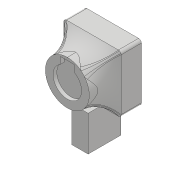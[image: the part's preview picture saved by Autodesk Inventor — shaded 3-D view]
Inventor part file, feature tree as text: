
AUTODESK INVENTOR PART (.ipt)
format: ipt  version: 2018 (Build 220112000, 112)  size: 754,176 bytes
history: native  units: mm
features: sketch x32, extrude x28, projected_geometry x28, fillet x4, hole x3, chamfer x1, mirror x1, revolve x1
ambient origin geometry x8: Origin, YZ Plane, XZ Plane, XY Plane, X Axis, Y Axis, Z Axis, Center Point
bodies: Solid1 (feature_tree)
feature tree (98):
  extrude  "Extrusion1"  Depth=45.0mm
  extrude  "Extrusion2"  Depth=2.25mm
  hole  "Hole1"  [1 undecoded]
  hole  "Hole2"  [1 undecoded]
  fillet  "Fillet1"  Radius=14.0mm
  extrude  "Extrusion3"  Depth=18.5mm
  extrude  "Extrusion4"  Depth=20.5mm
  extrude  "Extrusion5"  Depth=2.195mm
  extrude  "Extrusion6"  Depth=20.5mm
  hole  "Hole3"  [1 undecoded]
  extrude  "Extrusion7"  Depth=0.5mm
  extrude  "Extrusion8"  Depth=5.0mm TaperAngle=0.0deg
  extrude  "Extrusion9"  Depth=24.5mm
  extrude  "Extrusion10"  Depth=10.0mm
  extrude  "Extrusion11"  Depth=14.5mm
  extrude  "Extrusion12"  Depth=14.5mm
  extrude  "Extrusion13"  Depth=5.0mm
  extrude  "Extrusion14"  Depth=2.25mm
  extrude  "Extrusion15"  Depth=5.0mm
  extrude  "Extrusion16"  Depth=9.0mm
  extrude  "Extrusion17"  Depth=4.0mm
  chamfer  "Chamfer1"  Distance=1.0mm
  fillet  "Fillet8"  Radius=20.7mm
  mirror  "Mirror1"
  extrude  "Extrusion18"  Depth=32.0mm
  extrude  "Extrusion19"  Depth=1.0mm TaperAngle=0.0deg
  extrude  "Extrusion20"  Depth=8.0mm
  extrude  "Extrusion21"  Depth=0.2mm TaperAngle=0.0deg
  extrude  "Extrusion22"  Depth=0.5mm TaperAngle=0.0deg
  extrude  "Extrusion23"  Depth=3.0mm TaperAngle=0.0deg
  extrude  "Extrusion24"  Depth=0.2mm TaperAngle=0.0deg
  sketch  "Sketch35"  dims[d91=8.0mm d92=0.0mm d93=3.0mm d94=0.0mm]
  revolve  "Revolution1"  Angle=45.0deg
  extrude  "Extrusion25"  Depth=22.55mm TaperAngle=0.0deg
  fillet  "Fillet11"  Radius=4.0mm
  fillet  "Fillet14"  Radius=4.0mm
  extrude  "Extrusion33"  Depth=30.0mm
  extrude  "Extrusion34"  Depth=30.0mm TaperAngle=0.0deg
  extrude  "Extrusion35"  Depth=30.0mm
  sketch  "Sketch1"  dims[d0=24.5mm d1=45.0mm]
  sketch  "Sketch2"  dims[d2=1.95mm d3=0.0mm d4=2.25mm]
  projected_geometry  "Projected Loop1"
  sketch  "Sketch3"  dims[d5=20.0mm d6=2.25mm]
  projected_geometry  "Projected Loop2"
  sketch  "Sketch4"  dims[d7=5.25mm d8=5.25mm d9=14.0mm]
  projected_geometry  "Projected Loop3"
  sketch  "Sketch5"  dims[d10=5.25mm d11=18.5mm]
  projected_geometry  "Projected Loop4"
  sketch  "Sketch6"  dims[d12=10.0mm d13=0.0mm d14=20.5mm]
  projected_geometry  "Projected Loop5"
  sketch  "Sketch7"  dims[d15=2.0mm d16=2.195mm]
  projected_geometry  "Projected Loop6"
  sketch  "Sketch8"  dims[d17=2.0mm]
  projected_geometry  "Projected Loop7"
  sketch  "Sketch9"  dims[d18=2.4mm d19=6.0mm d20=4.4mm d21=2.0mm d22=90.0deg d23=8.0mm d24=20.594885mm d25=20.5mm]
  projected_geometry  "Projected Loop8"
  projected_geometry  "Projected Loop9"
  sketch  "Sketch10"  dims[d26=26.65mm d27=2.0mm]
  projected_geometry  "Projected Loop10"
  projected_geometry  "Projected Loop11"
  sketch  "Sketch11"  dims[d28=2.0mm]
  projected_geometry  "Projected Loop12"
  sketch  "Sketch12"  dims[d29=2.4mm d30=6.0mm d31=4.4mm d32=2.0mm d33=90.0deg d34=8.0mm d35=20.594885mm d36=0.5mm]
  sketch  "Sketch13"  dims[d37=18.0mm d38=5.0mm d39=0.0mm]
  sketch  "Sketch14"  dims[d41=10.0mm d42=0.0mm d43=24.5mm]
  projected_geometry  "Projected Loop13"
  sketch  "Sketch15"  dims[d44=1.15mm d45=0.0mm d46=10.0mm]
  sketch  "Sketch16"  dims[d47=21.0mm d48=14.5mm]
  projected_geometry  "Projected Loop14"
  sketch  "Sketch17"  dims[d49=20.0mm d50=14.5mm]
  projected_geometry  "Projected Loop15"
  sketch  "Sketch18"  dims[d51=24.5mm d52=5.0mm]
  projected_geometry  "Projected Loop16"
  sketch  "Sketch19"  dims[d53=5.0mm d54=2.25mm]
  projected_geometry  "Projected Loop17"
  sketch  "Sketch20"  dims[d55=2.25mm d56=5.0mm]
  projected_geometry  "Projected Loop18"
  sketch  "Sketch22"  dims[d57=5.0mm d58=9.0mm]
  sketch  "Sketch25"  dims[d59=14.75mm d60=4.0mm d61=1.0mm d62=0.0mm d63=20.7mm]
  sketch  "Sketch27"  dims[d64=2.4mm d65=6.0mm d66=4.4mm d67=2.0mm d68=90.0deg d69=8.0mm d70=20.594885mm d72=32.0mm]
  projected_geometry  "Projected Loop22"
  sketch  "Sketch28"  dims[d73=5.0mm d74=0.0mm d75=1.0mm d76=0.0mm]
  projected_geometry  "Projected Loop23"
  sketch  "Sketch29"  dims[d77=12.25mm d78=0.0mm d80=8.0mm]
  projected_geometry  "Projected Loop24"
  sketch  "Sketch30"  dims[d81=4.5mm d82=0.0mm d84=0.2mm d85=0.0mm]
  projected_geometry  "Projected Loop25"
  sketch  "Sketch33"  dims[d86=21.0mm d87=0.5mm d88=0.0mm]
  projected_geometry  "Projected Loop26"
  sketch  "Sketch36"  dims[d95=5.0mm d96=0.0mm d98=0.2mm d99=0.0mm]
  projected_geometry  "Projected Loop27"
  sketch  "Sketch45"  dims[d100=0.2mm d101=0.0mm d102=2.5mm d103=2.0mm d104=45.0deg]
  projected_geometry  "Projected Loop39"
  sketch  "Sketch46"  dims[d114=0.5mm d115=22.55mm d116=0.0mm d128=4.0mm d129=0.0mm d130=4.0mm d131=0.0mm]
  projected_geometry  "Projected Loop40"
  sketch  "Sketch47"  dims[d132=19.2mm d133=0.0mm d134=52.1mm d135=6.8mm d136=0.0mm d137=9.0mm d138=9.0mm d139=25.0mm d140=6.9mm d141=0.0mm d142=5.2mm d143=5.2mm d144=5.2mm d145=5.2mm d146=2.5mm d147=0.0mm d148=5.0mm d149=90.0deg d150=5.0mm d151=105.0mm d152=105.0mm d153=5.0mm d154=0.0mm d191=5.1mm d194=50.0mm d226=10.0mm d227=0.0mm d228=28.0mm d229=32.0mm d230=0.0mm d231=30.0mm d232=117.3mm d233=60.0mm d234=0.0mm]
  projected_geometry  "Projected Loop41"
  projected_geometry  "Project Cut Edges1"
note: 3 required parameter values undecoded (feature->parameter linkage not recoverable at this tier; creation-order binding heuristic only, values carry confidence <= 0.55)
